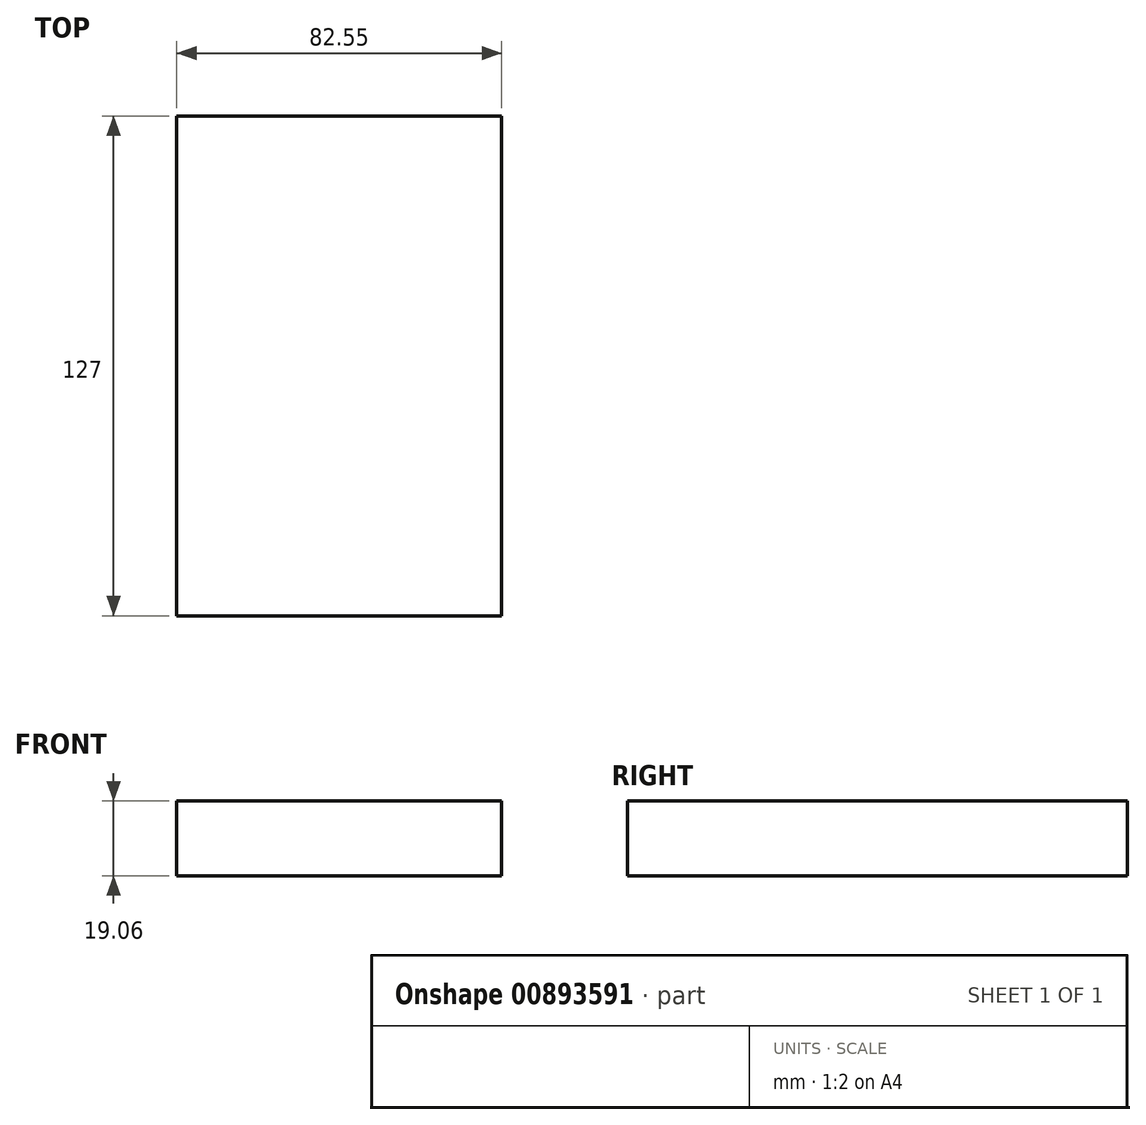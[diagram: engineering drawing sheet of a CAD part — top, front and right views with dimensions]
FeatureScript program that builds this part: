
annotation { "Feature Type Name" : "Feature", "Feature Type Description" : "" }
export const myFeature = defineFeature(function(context is Context, id is Id, definition is map)
    precondition{}
    {
        {
            var Q0;
            Q0=qCreatedBy(makeId("Front.planeOp"),FACE);
            var sketch = newSketch(context, id + "F0", { "sketchPlane" : qUnion([Q0])});
            skLineSegment(sketch, "E0.bottom", {"start": v(41.28, 9.53) * mm, "end": v(-41.28, 9.53) * mm});
            skLineSegment(sketch, "E0.top", {"start": v(41.28, -9.52) * mm, "end": v(-41.28, -9.52) * mm});
            skLineSegment(sketch, "E0.left", {"start": v(41.28, 9.53) * mm, "end": v(41.28, -9.52) * mm});
            skLineSegment(sketch, "E0.right", {"start": v(-41.28, 9.53) * mm, "end": v(-41.28, -9.52) * mm});
            skPoint(sketch, "E0.middle", {"position": v(0, 0) * mm});
            skLineSegment(sketch, "E1.bottom", {"start": v(60.32, 38.1) * mm, "end": v(111.12, 38.1) * mm});
            skLineSegment(sketch, "E1.top", {"start": v(60.32, 66.68) * mm, "end": v(111.12, 66.68) * mm});
            skLineSegment(sketch, "E1.left", {"start": v(60.32, 38.1) * mm, "end": v(60.32, 66.68) * mm});
            skLineSegment(sketch, "E1.right", {"start": v(111.12, 38.1) * mm, "end": v(111.12, 66.68) * mm});
            skPoint(sketch, "E1.middle", {"position": v(85.72, 52.39) * mm});
            skLineSegment(sketch, "E2", {"start": v(41.27, 9.53) * mm, "end": v(41.27, 27) * mm});
            skArc(sketch, "E3", {"start": v(41.27, 27) * mm, "mid": v(45.92, 38.23) * mm, "end": v(57.15, 42.88) * mm});
            skLineSegment(sketch, "E4", {"start": v(57.15, 42.88) * mm, "end": v(86.28, 42.88) * mm});
            skLineSegment(sketch, "E5.0", {"start": v(57.15, 61.93) * mm, "end": v(86.28, 61.93) * mm});
            skArc(sketch, "E5.1", {"start": v(22.22, 27) * mm, "mid": v(32.45, 51.7) * mm, "end": v(57.15, 61.93) * mm});
            skLineSegment(sketch, "E5.2", {"start": v(22.22, 9.53) * mm, "end": v(22.22, 27) * mm});
            skLineSegment(sketch, "E6", {"start": v(85.72, 66.68) * mm, "end": v(86.28, 38.1) * mm});
            skFitSpline(sketch, "E7", {"points": [v(-41.28, 9.52) * mm, v(57.15, 61.93) * mm], "startDerivative": vector(62.44, 114.41) * mm, "endDerivative": vector(113.97, -10.43) * mm});
            skSolve(sketch);
        }
        {
            var Q0;
            Q0=makeQuery(id+"F0.imprint","IMPRINT",FACE,{"disambiguationData":[TD([[makeQuery(id+"F0.imprint","IMPRINT",EDGE,{"derivedFrom":sQuery(id+"F0.wireOp",EDGE,"E0.top")}),-1.0]])]});
            extrude(context, id + "F1", {"entities" : qUnion([Q0]), "depth" : 127 * mm, "offsetDistance" : 25.4 * mm});
        }
    });
